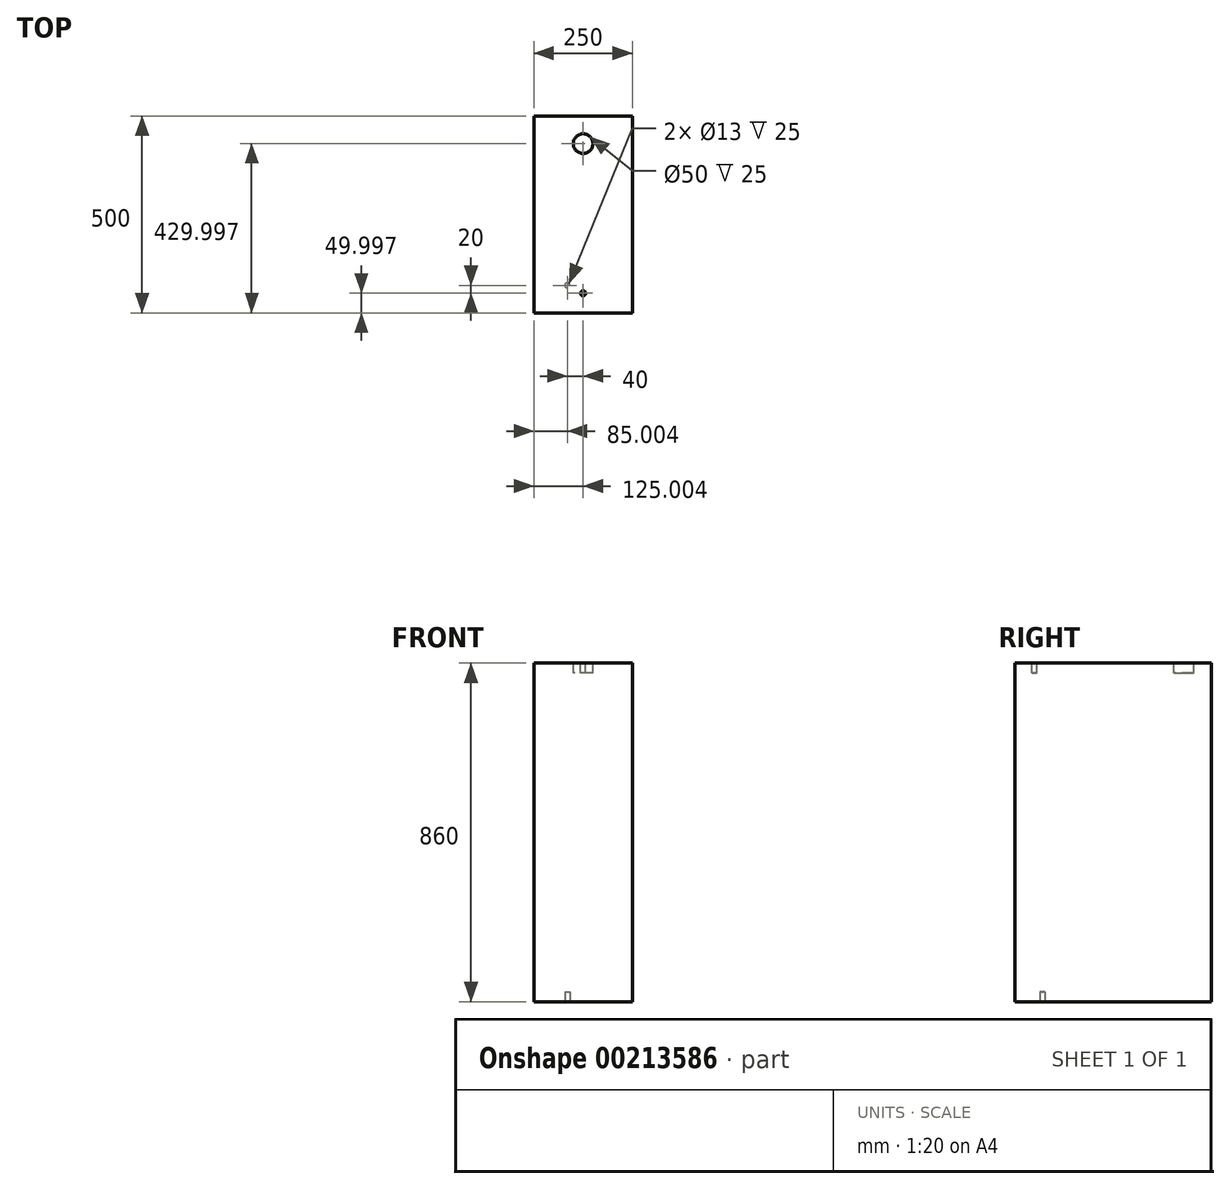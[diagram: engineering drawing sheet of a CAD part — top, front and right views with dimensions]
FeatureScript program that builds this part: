
annotation { "Feature Type Name" : "Feature", "Feature Type Description" : "" }
export const myFeature = defineFeature(function(context is Context, id is Id, definition is map)
    precondition{}
    {
        {
            var Q0;
            Q0=qCreatedBy(makeId("Top.planeOp"),FACE);
            var sketch = newSketch(context, id + "F0", { "sketchPlane" : qUnion([Q0])});
            skLineSegment(sketch, "E0.bottom", {"start": v(-120.45, 442.68) * mm, "end": v(129.55, 442.68) * mm});
            skLineSegment(sketch, "E0.top", {"start": v(-120.45, -57.32) * mm, "end": v(129.55, -57.32) * mm});
            skLineSegment(sketch, "E0.left", {"start": v(-120.45, 442.68) * mm, "end": v(-120.45, -57.32) * mm});
            skLineSegment(sketch, "E0.right", {"start": v(129.55, 442.68) * mm, "end": v(129.55, -57.32) * mm});
            skSolve(sketch);
        }
        {
            var Q0;
            Q0 = qSketchRegion(id + "F0", true);
            extrude(context, id + "F1", {"entities" : qUnion([Q0]), "depth" : 860 * mm});
        }
        {
            var Q0;
            Q0=makeQuery(id+"F1.opExtrude","CAP_FACE",FACE,{"disambiguationData":[OSD([sQuery(id+"F0.wireOp",EDGE,"E0.bottom"),sQuery(id+"F0.wireOp",EDGE,"E0.top"),sQuery(id+"F0.wireOp",EDGE,"E0.left"),sQuery(id+"F0.wireOp",EDGE,"E0.right")])],"isStart":false});
            var sketch = newSketch(context, id + "F2", { "sketchPlane" : qUnion([Q0])});
            skPoint(sketch, "E1.centerSnap0", {"position": v(4.55, -57.32) * mm});
            skPoint(sketch, "E1.centerSnap1", {"position": v(-120.45, 192.68) * mm});
            skCircle(sketch, "E2", {"center": v(4.55, 372.68) * mm, "radius": 25 * mm});
            skPoint(sketch, "E2.centerSnap0", {"position": v(4.55, 442.68) * mm});
            skCircle(sketch, "E3", {"center": v(4.55, -7.32) * mm, "radius": 6.5 * mm});
            skSolve(sketch);
        }
        {
            var Q0;
            Q0 = qSketchRegion(id + "F2", true);
            extrude(context, id + "F3", {"entities" : qUnion([Q0]), "operationType" : NewBodyOperationType.REMOVE, "oppositeDirection" : true, "depth" : 25 * mm});
        }
        {
            var Q0;
            Q0=makeQuery(id+"F1.opExtrude","CAP_FACE",FACE,{"disambiguationData":[OSD([sQuery(id+"F0.wireOp",EDGE,"E0.bottom"),sQuery(id+"F0.wireOp",EDGE,"E0.top"),sQuery(id+"F0.wireOp",EDGE,"E0.left"),sQuery(id+"F0.wireOp",EDGE,"E0.right")])],"isStart":true});
            var sketch = newSketch(context, id + "F4", { "sketchPlane" : qUnion([Q0])});
            skCircle(sketch, "E4", {"center": v(-35.45, -12.68) * mm, "radius": 6.5 * mm});
            skSolve(sketch);
        }
        {
            var Q0;
            Q0 = qSketchRegion(id + "F4", true);
            extrude(context, id + "F5", {"entities" : qUnion([Q0]), "operationType" : NewBodyOperationType.REMOVE, "oppositeDirection" : true, "depth" : 25 * mm});
        }
    });
